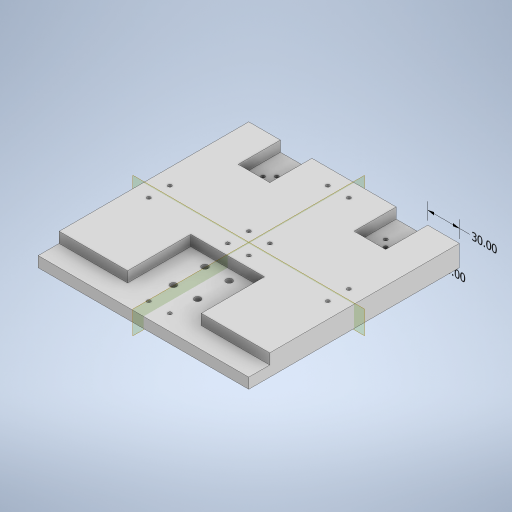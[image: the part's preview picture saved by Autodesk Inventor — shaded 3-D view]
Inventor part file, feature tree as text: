
AUTODESK INVENTOR PART (.ipt)
format: ipt  version: 2023 (Build 270158000, 158)  size: 364,032 bytes
history: native  units: mm
features: sketch x8, extrude x5, other x4, hole x3, plane x2
ambient origin geometry x8: Origin, YZ Plane, XZ Plane, XY Plane, X Axis, Y Axis, Z Axis, Center Point
bodies: Body1 (feature_tree)
feature tree (22):
  other  "Sólido1"
  other  "Anotaciones"
  extrude  "Extrusión1"  Depth=200.0mm
  extrude  "Extrusión2"  Depth=10.0mm TaperAngle=0.0deg
  extrude  "Extrusión3"  Depth=20.0mm
  hole  "Agujero1"  [1 undecoded]
  extrude  "Extrusión4"  Depth=10.0mm
  plane  "Plano de trabajo1"
  plane  "Plano de trabajo2"
  hole  "Agujero2"  [1 undecoded]
  extrude  "Extrusión5"  Depth=10.0mm TaperAngle=0.0deg
  hole  "Agujero3"  [1 undecoded]
  sketch  "Boceto1"  dims[d0=200.0mm d1=200.0mm]
  sketch  "Boceto2"  dims[d2=20.0mm d3=0.0mm]
  sketch  "Boceto3"  dims[d4=20.0mm d5=20.0mm d6=30.0mm d7=30.0mm d8=20.0mm d9=35.0mm d10=35.0mm d11=60.0mm d12=10.0mm d13=0.0mm]
  sketch  "Boceto4"  dims[d14=20.0mm d15=0.0mm]
  sketch  "Boceto5"  dims[d16=3.5mm d18=1.75mm d19=1.75mm d20=1.75mm d21=1.75mm d22=10.0mm d23=10.0mm d25=20.0mm]
  sketch  "Boceto7"  dims[d26=40.0mm d27=40.0mm]
  sketch  "Boceto8"  dims[d28=3.5mm d29=6.0mm d30=4.0mm d31=2.0mm d32=90.0deg d33=8.0mm d34=20.594885mm d38=10.0mm]
  sketch  "Boceto9"  dims[d39=10.0mm d40=40.0mm d41=10.0mm d42=0.0mm d52=3.5mm d54=10.0mm d55=10.0mm d56=3.5mm d57=6.0mm d58=4.0mm d59=2.0mm d60=90.0deg d61=8.0mm d62=20.594885mm d63=30.0mm d64=30.0mm d65=10.0mm d66=0.0mm d67=3.5mm d68=15.0mm d69=10.0mm d70=45.0deg d71=45.0deg d72=3.5mm d73=6.0mm d74=4.0mm d75=2.0mm d76=90.0deg d77=8.0mm d78=20.594885mm d43=6.672192mm d44=4.931866mm d45=30.0mm d46=5.890777mm d47=4.508932mm d48=30.0mm d83=0.5mm d84=0.872665mm d85=0.5mm d86=0.872665mm]
  other  "Cota lineal 1"
  other  "Cota lineal 2"
note: 3 required parameter values undecoded (feature->parameter linkage not recoverable at this tier; creation-order binding heuristic only, values carry confidence <= 0.55)
